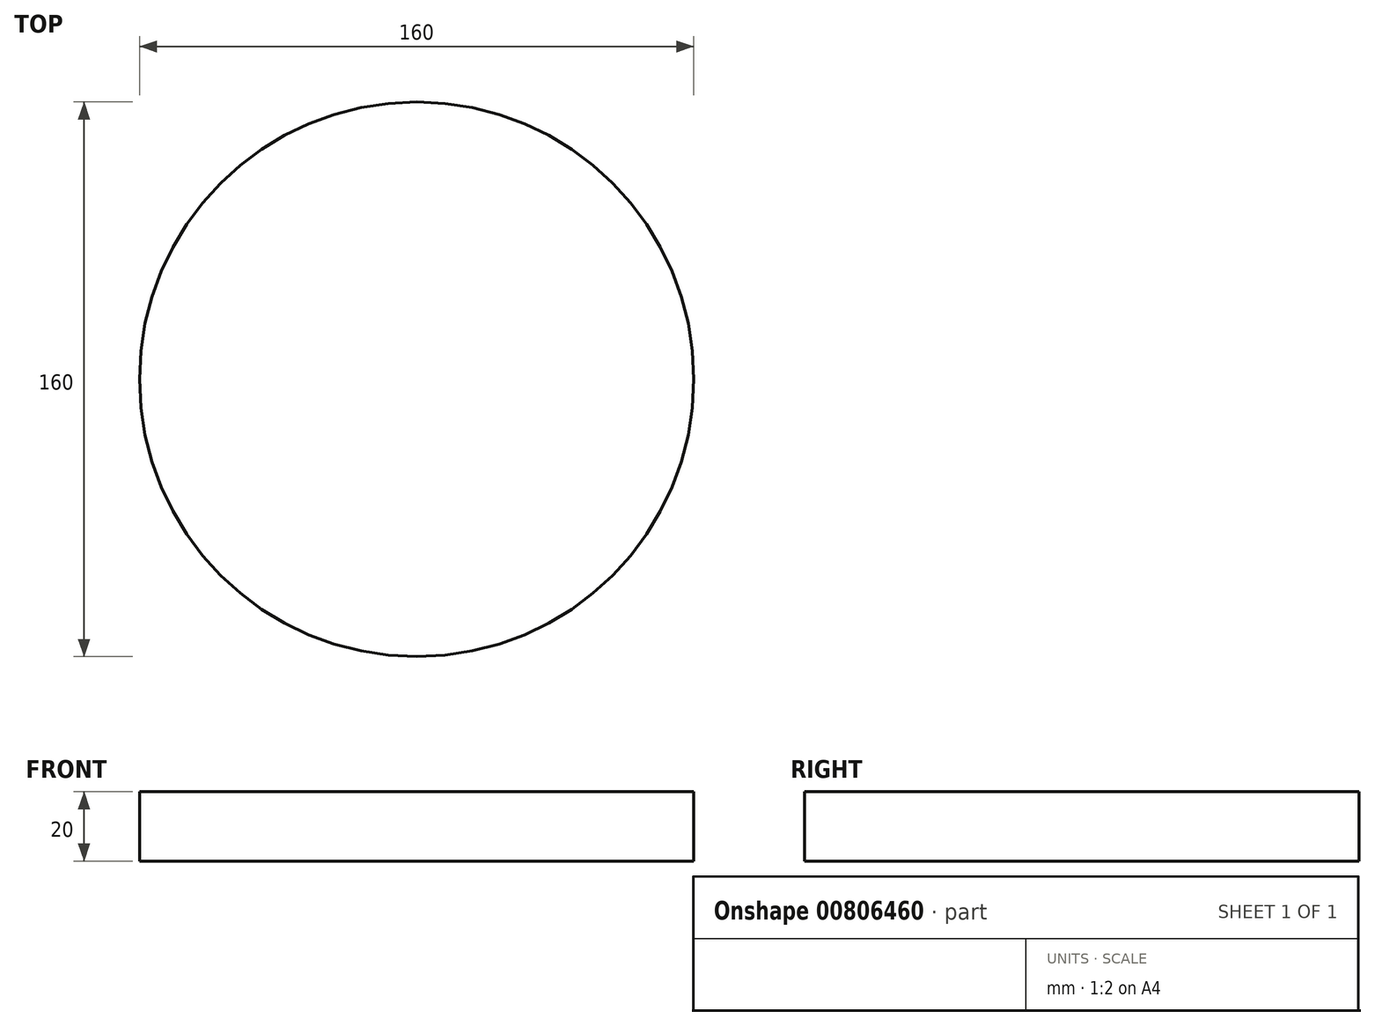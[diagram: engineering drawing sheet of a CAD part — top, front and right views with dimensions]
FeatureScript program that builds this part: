
annotation { "Feature Type Name" : "Feature", "Feature Type Description" : "" }
export const myFeature = defineFeature(function(context is Context, id is Id, definition is map)
    precondition{}
    {
        {
            var Q0;
            Q0=qCreatedBy(makeId("Top.planeOp"),FACE);
            var sketch = newSketch(context, id + "F0", { "sketchPlane" : qUnion([Q0])});
            skCircle(sketch, "E0", {"center": v(0, 0) * mm, "radius": 80 * mm});
            skSolve(sketch);
        }
        {
            var Q0;
            Q0=qSketchRegion(id+"F0",true);
            extrude(context, id + "F1", {"entities" : qUnion([Q0]), "depth" : 20 * mm, "offsetDistance" : 25 * mm});
        }
    });
